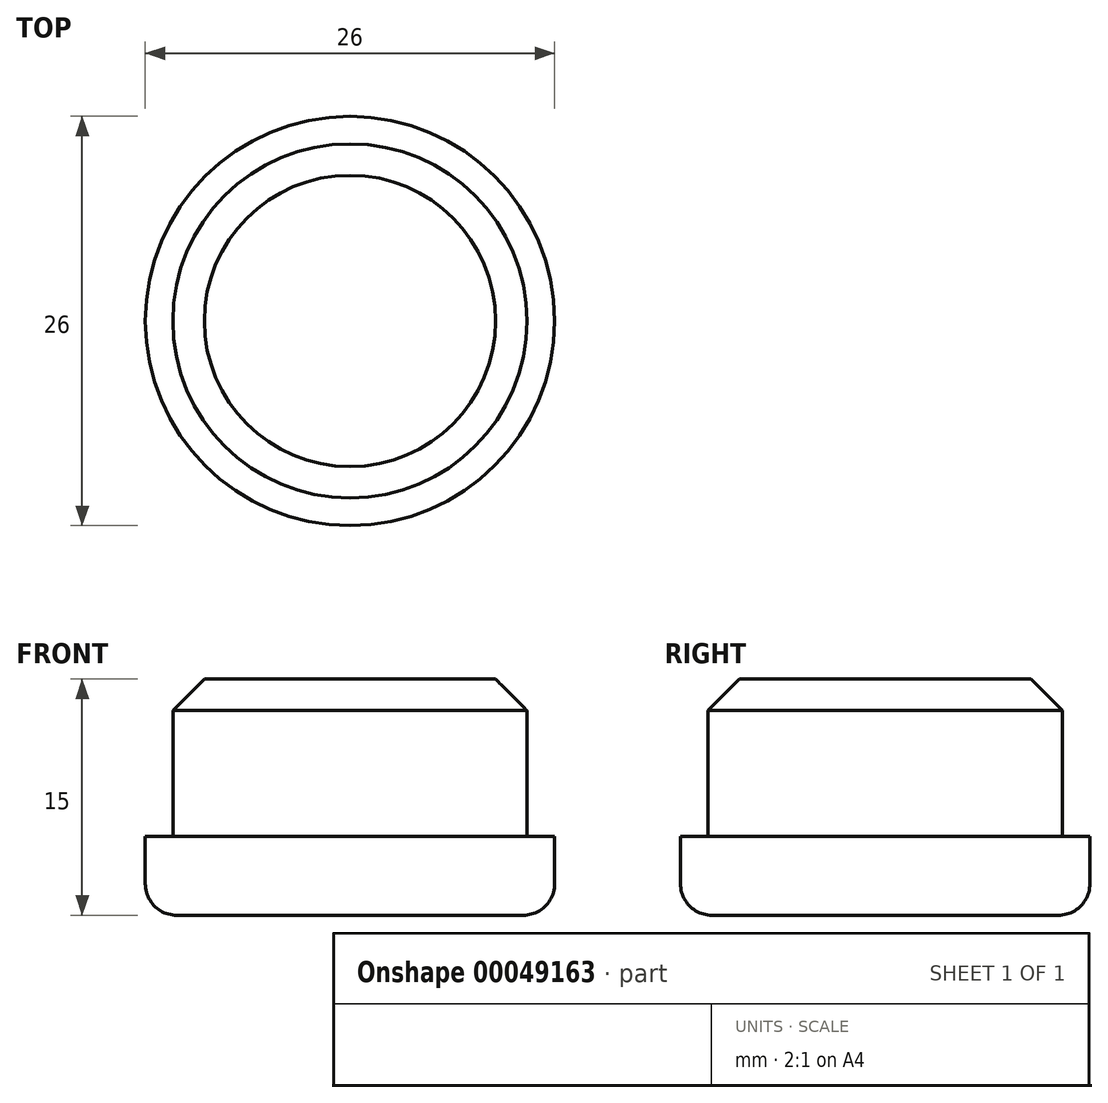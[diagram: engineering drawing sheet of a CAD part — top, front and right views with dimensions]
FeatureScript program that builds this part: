
annotation { "Feature Type Name" : "Feature", "Feature Type Description" : "" }
export const myFeature = defineFeature(function(context is Context, id is Id, definition is map)
    precondition{}
    {
        {
            var Q0;
            Q0=qCreatedBy(makeId("Top.planeOp"),FACE);
            var sketch = newSketch(context, id + "F0", { "sketchPlane" : qUnion([Q0])});
            skCircle(sketch, "E0", {"center": v(-1.53, 1.9) * mm, "radius": 11.25 * mm});
            skCircle(sketch, "E1", {"center": v(-1.53, 1.9) * mm, "radius": 13 * mm});
            skSolve(sketch);
        }
        {
            var Q0;
            Q0=makeQuery(id+"F0.imprint","IMPRINT",FACE,{"disambiguationData":[TD([[makeQuery(id+"F0.imprint","IMPRINT",EDGE,{"derivedFrom":sQuery(id+"F0.wireOp",EDGE,"E0")}),-1.0]])]});
            extrude(context, id + "F1", {"entities" : qUnion([Q0]), "depth" : 5 * mm});
        }
        {
            var Q0;
            Q0=makeQuery(id+"F0.imprint","IMPRINT",FACE,{"disambiguationData":[TD([[makeQuery(id+"F0.imprint","IMPRINT",EDGE,{"derivedFrom":sQuery(id+"F0.wireOp",EDGE,"E0")}),1.0]])]});
            extrude(context, id + "F2", {"entities" : qUnion([Q0]), "operationType" : NewBodyOperationType.ADD, "depth" : 15 * mm});
        }
        {
            var Q0;
            Q0=makeQuery(id+"F2.opExtrude","CAP_EDGE",EDGE,{"disambiguationData":[OSD([sQuery(id+"F0.wireOp",EDGE,"E0")])],"isStart":false});
            chamfer(context, id + "F3", {"entities" : qUnion([Q0]), "width" : 2 * mm, "tangentPropagation" : true});
        }
        {
            var Q0;
            Q0=makeQuery(id+"F1.opExtrude","CAP_EDGE",EDGE,{"disambiguationData":[OSD([sQuery(id+"F0.wireOp",EDGE,"E1")])],"isStart":true});
            fillet(context, id + "F4", {"entities" : qUnion([Q0]), "radius" : 2 * mm, "tangentPropagation" : true, "allowEdgeOverflow" : false});
        }
    });
